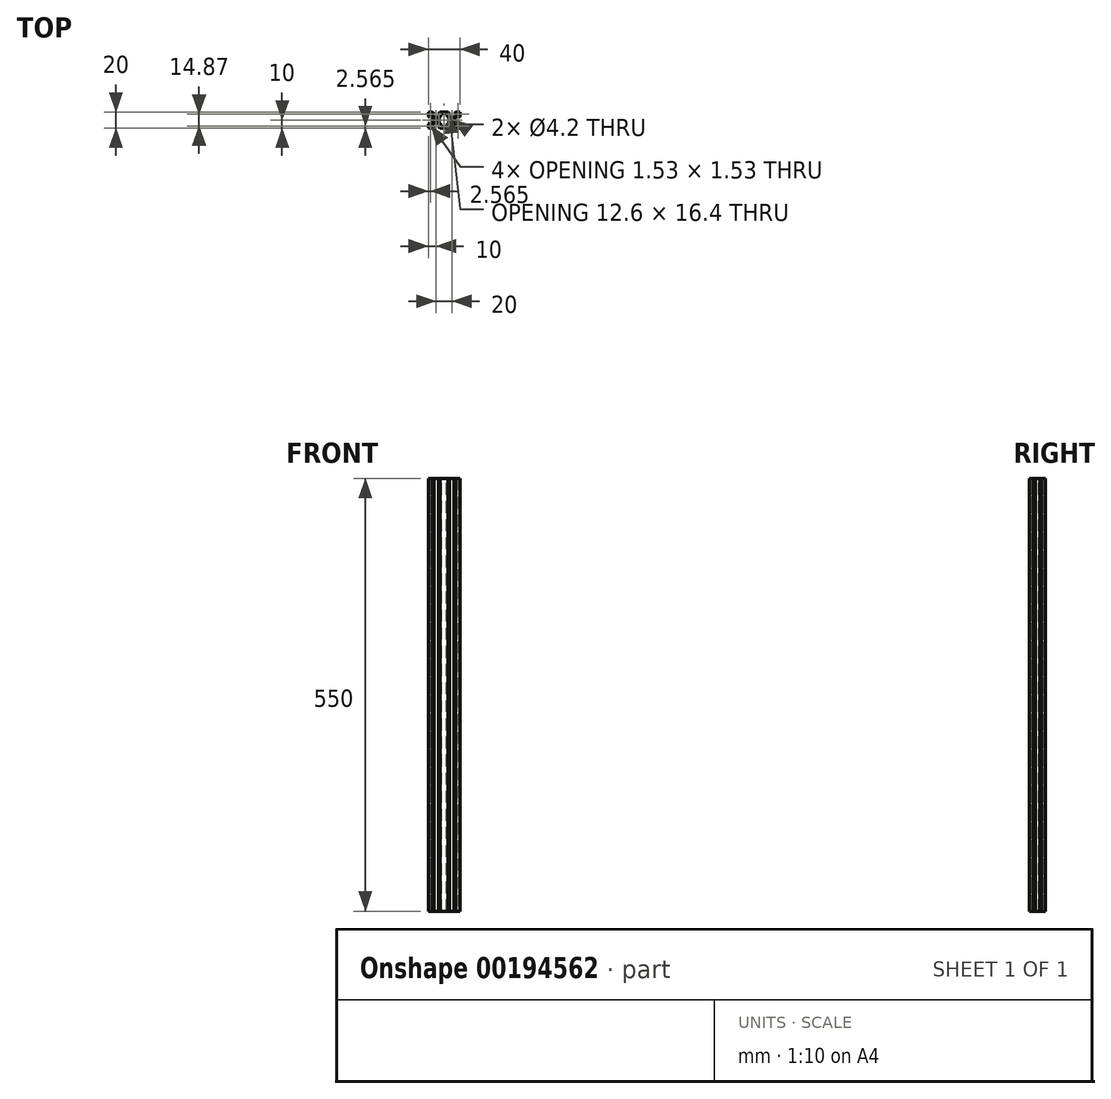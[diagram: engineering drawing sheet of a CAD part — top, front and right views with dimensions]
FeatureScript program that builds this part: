
annotation { "Feature Type Name" : "Feature", "Feature Type Description" : "" }
export const myFeature = defineFeature(function(context is Context, id is Id, definition is map)
    precondition{}
    {
        {
            var Q0;
            Q0=qCreatedBy(makeId("Top.planeOp"),FACE);
            var sketch = newSketch(context, id + "F0", { "sketchPlane" : qUnion([Q0])});
            skLineSegment(sketch, "E0.bottom", {"start": v(0, 0) * mm, "end": v(5.2, 0) * mm});
            skLineSegment(sketch, "E0.top", {"start": v(0, 20) * mm, "end": v(5.2, 20) * mm});
            skLineSegment(sketch, "E0.left", {"start": v(0, 0) * mm, "end": v(0, 5.2) * mm});
            skLineSegment(sketch, "E0.right", {"start": v(40, 0) * mm, "end": v(40, 5.2) * mm});
            skLineSegment(sketch, "E1", {"start": v(33.8, 12.84) * mm, "end": v(33.8, 7.16) * mm});
            skLineSegment(sketch, "E2", {"start": v(33.8, 12.84) * mm, "end": v(36.56, 15.6) * mm});
            skLineSegment(sketch, "E3", {"start": v(33.8, 7.16) * mm, "end": v(36.56, 4.4) * mm});
            skLineSegment(sketch, "E4", {"start": v(36.56, 15.6) * mm, "end": v(38.2, 15.6) * mm});
            skLineSegment(sketch, "E5", {"start": v(36.56, 4.4) * mm, "end": v(38.2, 4.4) * mm});
            skLineSegment(sketch, "E6", {"start": v(38.2, 13) * mm, "end": v(38.2, 15.6) * mm});
            skLineSegment(sketch, "E7", {"start": v(38.2, 7) * mm, "end": v(38.2, 4.4) * mm});
            skLineSegment(sketch, "E8.trimOffspring", {"start": v(40, 14.8) * mm, "end": v(40, 20) * mm});
            skLineSegment(sketch, "E9", {"start": v(33, 18.2) * mm, "end": v(35.6, 18.2) * mm});
            skLineSegment(sketch, "E10", {"start": v(35.6, 18.2) * mm, "end": v(35.6, 16.56) * mm});
            skLineSegment(sketch, "E11", {"start": v(35.6, 16.56) * mm, "end": v(32.84, 13.8) * mm});
            skLineSegment(sketch, "E12", {"start": v(32.84, 13.8) * mm, "end": v(27.16, 13.8) * mm});
            skLineSegment(sketch, "E13", {"start": v(27, 18.2) * mm, "end": v(24.4, 18.2) * mm});
            skLineSegment(sketch, "E14", {"start": v(24.4, 18.2) * mm, "end": v(24.4, 16.56) * mm});
            skLineSegment(sketch, "E15", {"start": v(24.4, 16.56) * mm, "end": v(27.16, 13.8) * mm});
            skLineSegment(sketch, "E16", {"start": v(33, 1.8) * mm, "end": v(35.6, 1.8) * mm});
            skLineSegment(sketch, "E17", {"start": v(35.6, 1.8) * mm, "end": v(35.6, 3.44) * mm});
            skLineSegment(sketch, "E18", {"start": v(35.6, 3.44) * mm, "end": v(32.84, 6.2) * mm});
            skLineSegment(sketch, "E19", {"start": v(32.84, 6.2) * mm, "end": v(27.16, 6.2) * mm});
            skLineSegment(sketch, "E20", {"start": v(27.16, 6.2) * mm, "end": v(24.4, 3.44) * mm});
            skLineSegment(sketch, "E21", {"start": v(24.4, 3.44) * mm, "end": v(24.4, 1.8) * mm});
            skLineSegment(sketch, "E22", {"start": v(24.4, 1.8) * mm, "end": v(27, 1.8) * mm});
            skLineSegment(sketch, "E23.trimOffspring", {"start": v(34.8, 20) * mm, "end": v(40, 20) * mm});
            skLineSegment(sketch, "E24.trimOffspring", {"start": v(34.8, 0) * mm, "end": v(40, 0) * mm});
            skLineSegment(sketch, "E25", {"start": v(7, 18.2) * mm, "end": v(4.4, 18.2) * mm});
            skLineSegment(sketch, "E26", {"start": v(4.4, 18.2) * mm, "end": v(4.4, 16.56) * mm});
            skLineSegment(sketch, "E27", {"start": v(4.4, 16.56) * mm, "end": v(7.16, 13.8) * mm});
            skLineSegment(sketch, "E28", {"start": v(7.16, 13.8) * mm, "end": v(12.84, 13.8) * mm});
            skLineSegment(sketch, "E29", {"start": v(12.84, 13.8) * mm, "end": v(15.6, 16.56) * mm});
            skLineSegment(sketch, "E30", {"start": v(15.6, 16.56) * mm, "end": v(15.6, 18.2) * mm});
            skLineSegment(sketch, "E31", {"start": v(15.6, 18.2) * mm, "end": v(13, 18.2) * mm});
            skLineSegment(sketch, "E32", {"start": v(1.8, 13) * mm, "end": v(1.8, 15.6) * mm});
            skLineSegment(sketch, "E33", {"start": v(1.8, 15.6) * mm, "end": v(3.44, 15.6) * mm});
            skLineSegment(sketch, "E34", {"start": v(3.44, 15.6) * mm, "end": v(6.2, 12.84) * mm});
            skLineSegment(sketch, "E35", {"start": v(6.2, 12.84) * mm, "end": v(6.2, 7.16) * mm});
            skLineSegment(sketch, "E36", {"start": v(6.2, 7.16) * mm, "end": v(3.44, 4.4) * mm});
            skLineSegment(sketch, "E37", {"start": v(3.44, 4.4) * mm, "end": v(1.8, 4.4) * mm});
            skLineSegment(sketch, "E38", {"start": v(1.8, 7) * mm, "end": v(1.8, 4.4) * mm});
            skLineSegment(sketch, "E39", {"start": v(7, 1.8) * mm, "end": v(4.4, 1.8) * mm});
            skLineSegment(sketch, "E40", {"start": v(4.4, 1.8) * mm, "end": v(4.4, 3.44) * mm});
            skLineSegment(sketch, "E41", {"start": v(4.4, 3.44) * mm, "end": v(7.16, 6.2) * mm});
            skLineSegment(sketch, "E42", {"start": v(7.16, 6.2) * mm, "end": v(12.84, 6.2) * mm});
            skLineSegment(sketch, "E43", {"start": v(12.84, 6.2) * mm, "end": v(15.6, 3.44) * mm});
            skLineSegment(sketch, "E44", {"start": v(15.6, 3.44) * mm, "end": v(15.6, 1.8) * mm});
            skLineSegment(sketch, "E45", {"start": v(15.6, 1.8) * mm, "end": v(13, 1.8) * mm});
            skLineSegment(sketch, "E46.trimOffspring", {"start": v(14.8, 20) * mm, "end": v(25.2, 20) * mm});
            skLineSegment(sketch, "E47.trimOffspring", {"start": v(0, 14.8) * mm, "end": v(0, 20) * mm});
            skLineSegment(sketch, "E48.trimOffspring", {"start": v(14.8, 0) * mm, "end": v(25.2, 0) * mm});
            skLineSegment(sketch, "E49", {"start": v(38.2, 7) * mm, "end": v(40, 5.2) * mm});
            skLineSegment(sketch, "E50", {"start": v(38.2, 13) * mm, "end": v(40, 14.8) * mm});
            skLineSegment(sketch, "E51", {"start": v(33, 1.8) * mm, "end": v(34.8, 0) * mm});
            skLineSegment(sketch, "E52", {"start": v(27, 1.8) * mm, "end": v(25.2, 0) * mm});
            skLineSegment(sketch, "E53", {"start": v(13, 1.8) * mm, "end": v(14.8, 0) * mm});
            skLineSegment(sketch, "E54", {"start": v(7, 1.8) * mm, "end": v(5.2, 0) * mm});
            skLineSegment(sketch, "E55", {"start": v(1.8, 7) * mm, "end": v(0, 5.2) * mm});
            skLineSegment(sketch, "E56", {"start": v(1.8, 13) * mm, "end": v(0, 14.8) * mm});
            skLineSegment(sketch, "E57", {"start": v(7, 18.2) * mm, "end": v(5.2, 20) * mm});
            skLineSegment(sketch, "E58", {"start": v(13, 18.2) * mm, "end": v(14.8, 20) * mm});
            skLineSegment(sketch, "E59", {"start": v(27, 18.2) * mm, "end": v(25.2, 20) * mm});
            skLineSegment(sketch, "E60", {"start": v(33, 18.2) * mm, "end": v(34.8, 20) * mm});
            skPoint(sketch, "E61.start.orphan", {"position": v(7, 0) * mm});
            skSolve(sketch);
        }
        {
            var Q0;
            Q0=qSketchRegion(id+"F0",true);
            extrude(context, id + "F1", {"entities" : qUnion([Q0]), "depth" : 1500 * mm});
        }
        {
            var Q0;
            Q0=makeQuery(id+"F1.opExtrude","CAP_FACE",FACE,{"disambiguationData":[OSD([sQuery(id+"F0.wireOp",EDGE,"E0.bottom"),sQuery(id+"F0.wireOp",EDGE,"E0.top"),sQuery(id+"F0.wireOp",EDGE,"E0.left"),sQuery(id+"F0.wireOp",EDGE,"E0.right"),sQuery(id+"F0.wireOp",EDGE,"E1"),sQuery(id+"F0.wireOp",EDGE,"E2"),sQuery(id+"F0.wireOp",EDGE,"E3"),sQuery(id+"F0.wireOp",EDGE,"E4"),sQuery(id+"F0.wireOp",EDGE,"E5"),sQuery(id+"F0.wireOp",EDGE,"E6"),sQuery(id+"F0.wireOp",EDGE,"E7"),sQuery(id+"F0.wireOp",EDGE,"E8.trimOffspring"),sQuery(id+"F0.wireOp",EDGE,"E9"),sQuery(id+"F0.wireOp",EDGE,"E10"),sQuery(id+"F0.wireOp",EDGE,"E11"),sQuery(id+"F0.wireOp",EDGE,"E12"),sQuery(id+"F0.wireOp",EDGE,"E13"),sQuery(id+"F0.wireOp",EDGE,"E14"),sQuery(id+"F0.wireOp",EDGE,"E15"),sQuery(id+"F0.wireOp",EDGE,"E16"),sQuery(id+"F0.wireOp",EDGE,"E17"),sQuery(id+"F0.wireOp",EDGE,"E18"),sQuery(id+"F0.wireOp",EDGE,"E19"),sQuery(id+"F0.wireOp",EDGE,"E20"),sQuery(id+"F0.wireOp",EDGE,"E21"),sQuery(id+"F0.wireOp",EDGE,"E22"),sQuery(id+"F0.wireOp",EDGE,"E23.trimOffspring"),sQuery(id+"F0.wireOp",EDGE,"E24.trimOffspring"),sQuery(id+"F0.wireOp",EDGE,"E25"),sQuery(id+"F0.wireOp",EDGE,"E26"),sQuery(id+"F0.wireOp",EDGE,"E27"),sQuery(id+"F0.wireOp",EDGE,"E28"),sQuery(id+"F0.wireOp",EDGE,"E29"),sQuery(id+"F0.wireOp",EDGE,"E30"),sQuery(id+"F0.wireOp",EDGE,"E31"),sQuery(id+"F0.wireOp",EDGE,"E32"),sQuery(id+"F0.wireOp",EDGE,"E33"),sQuery(id+"F0.wireOp",EDGE,"E34"),sQuery(id+"F0.wireOp",EDGE,"E35"),sQuery(id+"F0.wireOp",EDGE,"E36"),sQuery(id+"F0.wireOp",EDGE,"E37"),sQuery(id+"F0.wireOp",EDGE,"E38"),sQuery(id+"F0.wireOp",EDGE,"E39"),sQuery(id+"F0.wireOp",EDGE,"E40"),sQuery(id+"F0.wireOp",EDGE,"E41"),sQuery(id+"F0.wireOp",EDGE,"E42"),sQuery(id+"F0.wireOp",EDGE,"E43"),sQuery(id+"F0.wireOp",EDGE,"E44"),sQuery(id+"F0.wireOp",EDGE,"E45"),sQuery(id+"F0.wireOp",EDGE,"E46.trimOffspring"),sQuery(id+"F0.wireOp",EDGE,"E47.trimOffspring"),sQuery(id+"F0.wireOp",EDGE,"E48.trimOffspring"),sQuery(id+"F0.wireOp",EDGE,"E49"),sQuery(id+"F0.wireOp",EDGE,"E50"),sQuery(id+"F0.wireOp",EDGE,"E51"),sQuery(id+"F0.wireOp",EDGE,"E52"),sQuery(id+"F0.wireOp",EDGE,"E53"),sQuery(id+"F0.wireOp",EDGE,"E54"),sQuery(id+"F0.wireOp",EDGE,"E55"),sQuery(id+"F0.wireOp",EDGE,"E56"),sQuery(id+"F0.wireOp",EDGE,"E57"),sQuery(id+"F0.wireOp",EDGE,"E58"),sQuery(id+"F0.wireOp",EDGE,"E59"),sQuery(id+"F0.wireOp",EDGE,"E60")])],"isStart":false});
            var sketch = newSketch(context, id + "F2", { "sketchPlane" : qUnion([Q0])});
            skLineSegment(sketch, "E62", {"start": v(1.8, 18.2) * mm, "end": v(1.8, 16.67) * mm});
            skLineSegment(sketch, "E63", {"start": v(1.8, 16.67) * mm, "end": v(3.33, 18.2) * mm});
            skLineSegment(sketch, "E64", {"start": v(3.33, 18.2) * mm, "end": v(1.8, 18.2) * mm});
            skLineSegment(sketch, "E65", {"start": v(1.8, 1.8) * mm, "end": v(3.33, 1.8) * mm});
            skLineSegment(sketch, "E66", {"start": v(3.33, 1.8) * mm, "end": v(1.8, 3.33) * mm});
            skLineSegment(sketch, "E67", {"start": v(1.8, 3.33) * mm, "end": v(1.8, 1.8) * mm});
            skLineSegment(sketch, "E68", {"start": v(38.2, 1.8) * mm, "end": v(38.2, 3.33) * mm});
            skLineSegment(sketch, "E69", {"start": v(38.2, 3.33) * mm, "end": v(36.67, 1.8) * mm});
            skLineSegment(sketch, "E70", {"start": v(36.67, 1.8) * mm, "end": v(38.2, 1.8) * mm});
            skLineSegment(sketch, "E71", {"start": v(38.2, 18.2) * mm, "end": v(38.2, 16.67) * mm});
            skLineSegment(sketch, "E72", {"start": v(38.2, 16.67) * mm, "end": v(36.67, 18.2) * mm});
            skLineSegment(sketch, "E73", {"start": v(36.67, 18.2) * mm, "end": v(38.2, 18.2) * mm});
            skSolve(sketch);
        }
        {
            var Q0;
            Q0=qSketchRegion(id+"F2",true);
            extrude(context, id + "F3", {"entities" : qUnion([Q0]), "operationType" : NewBodyOperationType.REMOVE, "endBound" : BoundingType.THROUGH_ALL, "oppositeDirection" : true, "depth" : 25 * mm});
        }
        {
            var Q0;
            Q0=makeQuery(id+"F1.opExtrude","CAP_FACE",FACE,{"disambiguationData":[OSD([sQuery(id+"F0.wireOp",EDGE,"E0.bottom"),sQuery(id+"F0.wireOp",EDGE,"E0.top"),sQuery(id+"F0.wireOp",EDGE,"E0.left"),sQuery(id+"F0.wireOp",EDGE,"E0.right"),sQuery(id+"F0.wireOp",EDGE,"E1"),sQuery(id+"F0.wireOp",EDGE,"E2"),sQuery(id+"F0.wireOp",EDGE,"E3"),sQuery(id+"F0.wireOp",EDGE,"E4"),sQuery(id+"F0.wireOp",EDGE,"E5"),sQuery(id+"F0.wireOp",EDGE,"E6"),sQuery(id+"F0.wireOp",EDGE,"E7"),sQuery(id+"F0.wireOp",EDGE,"E8.trimOffspring"),sQuery(id+"F0.wireOp",EDGE,"E9"),sQuery(id+"F0.wireOp",EDGE,"E10"),sQuery(id+"F0.wireOp",EDGE,"E11"),sQuery(id+"F0.wireOp",EDGE,"E12"),sQuery(id+"F0.wireOp",EDGE,"E13"),sQuery(id+"F0.wireOp",EDGE,"E14"),sQuery(id+"F0.wireOp",EDGE,"E15"),sQuery(id+"F0.wireOp",EDGE,"E16"),sQuery(id+"F0.wireOp",EDGE,"E17"),sQuery(id+"F0.wireOp",EDGE,"E18"),sQuery(id+"F0.wireOp",EDGE,"E19"),sQuery(id+"F0.wireOp",EDGE,"E20"),sQuery(id+"F0.wireOp",EDGE,"E21"),sQuery(id+"F0.wireOp",EDGE,"E22"),sQuery(id+"F0.wireOp",EDGE,"E23.trimOffspring"),sQuery(id+"F0.wireOp",EDGE,"E24.trimOffspring"),sQuery(id+"F0.wireOp",EDGE,"E25"),sQuery(id+"F0.wireOp",EDGE,"E26"),sQuery(id+"F0.wireOp",EDGE,"E27"),sQuery(id+"F0.wireOp",EDGE,"E28"),sQuery(id+"F0.wireOp",EDGE,"E29"),sQuery(id+"F0.wireOp",EDGE,"E30"),sQuery(id+"F0.wireOp",EDGE,"E31"),sQuery(id+"F0.wireOp",EDGE,"E32"),sQuery(id+"F0.wireOp",EDGE,"E33"),sQuery(id+"F0.wireOp",EDGE,"E34"),sQuery(id+"F0.wireOp",EDGE,"E35"),sQuery(id+"F0.wireOp",EDGE,"E36"),sQuery(id+"F0.wireOp",EDGE,"E37"),sQuery(id+"F0.wireOp",EDGE,"E38"),sQuery(id+"F0.wireOp",EDGE,"E39"),sQuery(id+"F0.wireOp",EDGE,"E40"),sQuery(id+"F0.wireOp",EDGE,"E41"),sQuery(id+"F0.wireOp",EDGE,"E42"),sQuery(id+"F0.wireOp",EDGE,"E43"),sQuery(id+"F0.wireOp",EDGE,"E44"),sQuery(id+"F0.wireOp",EDGE,"E45"),sQuery(id+"F0.wireOp",EDGE,"E46.trimOffspring"),sQuery(id+"F0.wireOp",EDGE,"E47.trimOffspring"),sQuery(id+"F0.wireOp",EDGE,"E48.trimOffspring"),sQuery(id+"F0.wireOp",EDGE,"E49"),sQuery(id+"F0.wireOp",EDGE,"E50"),sQuery(id+"F0.wireOp",EDGE,"E51"),sQuery(id+"F0.wireOp",EDGE,"E52"),sQuery(id+"F0.wireOp",EDGE,"E53"),sQuery(id+"F0.wireOp",EDGE,"E54"),sQuery(id+"F0.wireOp",EDGE,"E55"),sQuery(id+"F0.wireOp",EDGE,"E56"),sQuery(id+"F0.wireOp",EDGE,"E57"),sQuery(id+"F0.wireOp",EDGE,"E58"),sQuery(id+"F0.wireOp",EDGE,"E59"),sQuery(id+"F0.wireOp",EDGE,"E60")])],"isStart":false});
            var sketch = newSketch(context, id + "F4", { "sketchPlane" : qUnion([Q0])});
            skLineSegment(sketch, "E74", {"start": v(17.1, 18.2) * mm, "end": v(22.9, 18.2) * mm});
            skLineSegment(sketch, "E75", {"start": v(22.9, 1.8) * mm, "end": v(17.1, 1.8) * mm});
            skLineSegment(sketch, "E76", {"start": v(17.1, 1.8) * mm, "end": v(17.1, 3.76) * mm});
            skLineSegment(sketch, "E77", {"start": v(22.9, 1.8) * mm, "end": v(22.9, 3.76) * mm});
            skLineSegment(sketch, "E78", {"start": v(22.9, 18.2) * mm, "end": v(22.9, 16.24) * mm});
            skLineSegment(sketch, "E79", {"start": v(17.1, 18.2) * mm, "end": v(17.1, 16.24) * mm});
            skLineSegment(sketch, "E80", {"start": v(22.9, 16.24) * mm, "end": v(26.3, 12.84) * mm});
            skLineSegment(sketch, "E81", {"start": v(26.3, 12.84) * mm, "end": v(26.3, 7.16) * mm});
            skLineSegment(sketch, "E82", {"start": v(26.3, 7.16) * mm, "end": v(22.9, 3.76) * mm});
            skLineSegment(sketch, "E83", {"start": v(17.1, 3.76) * mm, "end": v(13.7, 7.16) * mm});
            skLineSegment(sketch, "E84", {"start": v(13.7, 7.16) * mm, "end": v(13.7, 12.84) * mm});
            skLineSegment(sketch, "E85", {"start": v(13.7, 12.84) * mm, "end": v(17.1, 16.24) * mm});
            skCircle(sketch, "E86", {"center": v(30, 10) * mm, "radius": 2.1 * mm});
            skPoint(sketch, "E86.centerSnap0", {"position": v(30, 13.8) * mm});
            skPoint(sketch, "E86.centerSnap1", {"position": v(26.3, 10) * mm});
            skCircle(sketch, "E87", {"center": v(10, 10) * mm, "radius": 2.1 * mm});
            skPoint(sketch, "E87.centerSnap0", {"position": v(10, 13.8) * mm});
            skPoint(sketch, "E87.centerSnap1", {"position": v(13.7, 10) * mm});
            skSolve(sketch);
        }
        {
            var Q0;
            Q0=qSketchRegion(id+"F4",true);
            extrude(context, id + "F5", {"entities" : qUnion([Q0]), "operationType" : NewBodyOperationType.REMOVE, "endBound" : BoundingType.THROUGH_ALL, "oppositeDirection" : true, "depth" : 25 * mm});
        }
        {
            var Q0;
            Q0=makeQuery(id+"F1.opExtrude","CAP_FACE",FACE,{"disambiguationData":[OSD([sQuery(id+"F0.wireOp",EDGE,"E0.bottom"),sQuery(id+"F0.wireOp",EDGE,"E0.top"),sQuery(id+"F0.wireOp",EDGE,"E0.left"),sQuery(id+"F0.wireOp",EDGE,"E0.right"),sQuery(id+"F0.wireOp",EDGE,"E1"),sQuery(id+"F0.wireOp",EDGE,"E2"),sQuery(id+"F0.wireOp",EDGE,"E3"),sQuery(id+"F0.wireOp",EDGE,"E4"),sQuery(id+"F0.wireOp",EDGE,"E5"),sQuery(id+"F0.wireOp",EDGE,"E6"),sQuery(id+"F0.wireOp",EDGE,"E7"),sQuery(id+"F0.wireOp",EDGE,"E8.trimOffspring"),sQuery(id+"F0.wireOp",EDGE,"E9"),sQuery(id+"F0.wireOp",EDGE,"E10"),sQuery(id+"F0.wireOp",EDGE,"E11"),sQuery(id+"F0.wireOp",EDGE,"E12"),sQuery(id+"F0.wireOp",EDGE,"E13"),sQuery(id+"F0.wireOp",EDGE,"E14"),sQuery(id+"F0.wireOp",EDGE,"E15"),sQuery(id+"F0.wireOp",EDGE,"E16"),sQuery(id+"F0.wireOp",EDGE,"E17"),sQuery(id+"F0.wireOp",EDGE,"E18"),sQuery(id+"F0.wireOp",EDGE,"E19"),sQuery(id+"F0.wireOp",EDGE,"E20"),sQuery(id+"F0.wireOp",EDGE,"E21"),sQuery(id+"F0.wireOp",EDGE,"E22"),sQuery(id+"F0.wireOp",EDGE,"E23.trimOffspring"),sQuery(id+"F0.wireOp",EDGE,"E24.trimOffspring"),sQuery(id+"F0.wireOp",EDGE,"E25"),sQuery(id+"F0.wireOp",EDGE,"E26"),sQuery(id+"F0.wireOp",EDGE,"E27"),sQuery(id+"F0.wireOp",EDGE,"E28"),sQuery(id+"F0.wireOp",EDGE,"E29"),sQuery(id+"F0.wireOp",EDGE,"E30"),sQuery(id+"F0.wireOp",EDGE,"E31"),sQuery(id+"F0.wireOp",EDGE,"E32"),sQuery(id+"F0.wireOp",EDGE,"E33"),sQuery(id+"F0.wireOp",EDGE,"E34"),sQuery(id+"F0.wireOp",EDGE,"E35"),sQuery(id+"F0.wireOp",EDGE,"E36"),sQuery(id+"F0.wireOp",EDGE,"E37"),sQuery(id+"F0.wireOp",EDGE,"E38"),sQuery(id+"F0.wireOp",EDGE,"E39"),sQuery(id+"F0.wireOp",EDGE,"E40"),sQuery(id+"F0.wireOp",EDGE,"E41"),sQuery(id+"F0.wireOp",EDGE,"E42"),sQuery(id+"F0.wireOp",EDGE,"E43"),sQuery(id+"F0.wireOp",EDGE,"E44"),sQuery(id+"F0.wireOp",EDGE,"E45"),sQuery(id+"F0.wireOp",EDGE,"E46.trimOffspring"),sQuery(id+"F0.wireOp",EDGE,"E47.trimOffspring"),sQuery(id+"F0.wireOp",EDGE,"E48.trimOffspring"),sQuery(id+"F0.wireOp",EDGE,"E49"),sQuery(id+"F0.wireOp",EDGE,"E50"),sQuery(id+"F0.wireOp",EDGE,"E51"),sQuery(id+"F0.wireOp",EDGE,"E52"),sQuery(id+"F0.wireOp",EDGE,"E53"),sQuery(id+"F0.wireOp",EDGE,"E54"),sQuery(id+"F0.wireOp",EDGE,"E55"),sQuery(id+"F0.wireOp",EDGE,"E56"),sQuery(id+"F0.wireOp",EDGE,"E57"),sQuery(id+"F0.wireOp",EDGE,"E58"),sQuery(id+"F0.wireOp",EDGE,"E59"),sQuery(id+"F0.wireOp",EDGE,"E60")])],"isStart":false});
            extrude(context, id + "F6", {"entities" : qUnion([Q0]), "operationType" : NewBodyOperationType.REMOVE, "oppositeDirection" : true, "depth" : 950 * mm});
        }
    });
